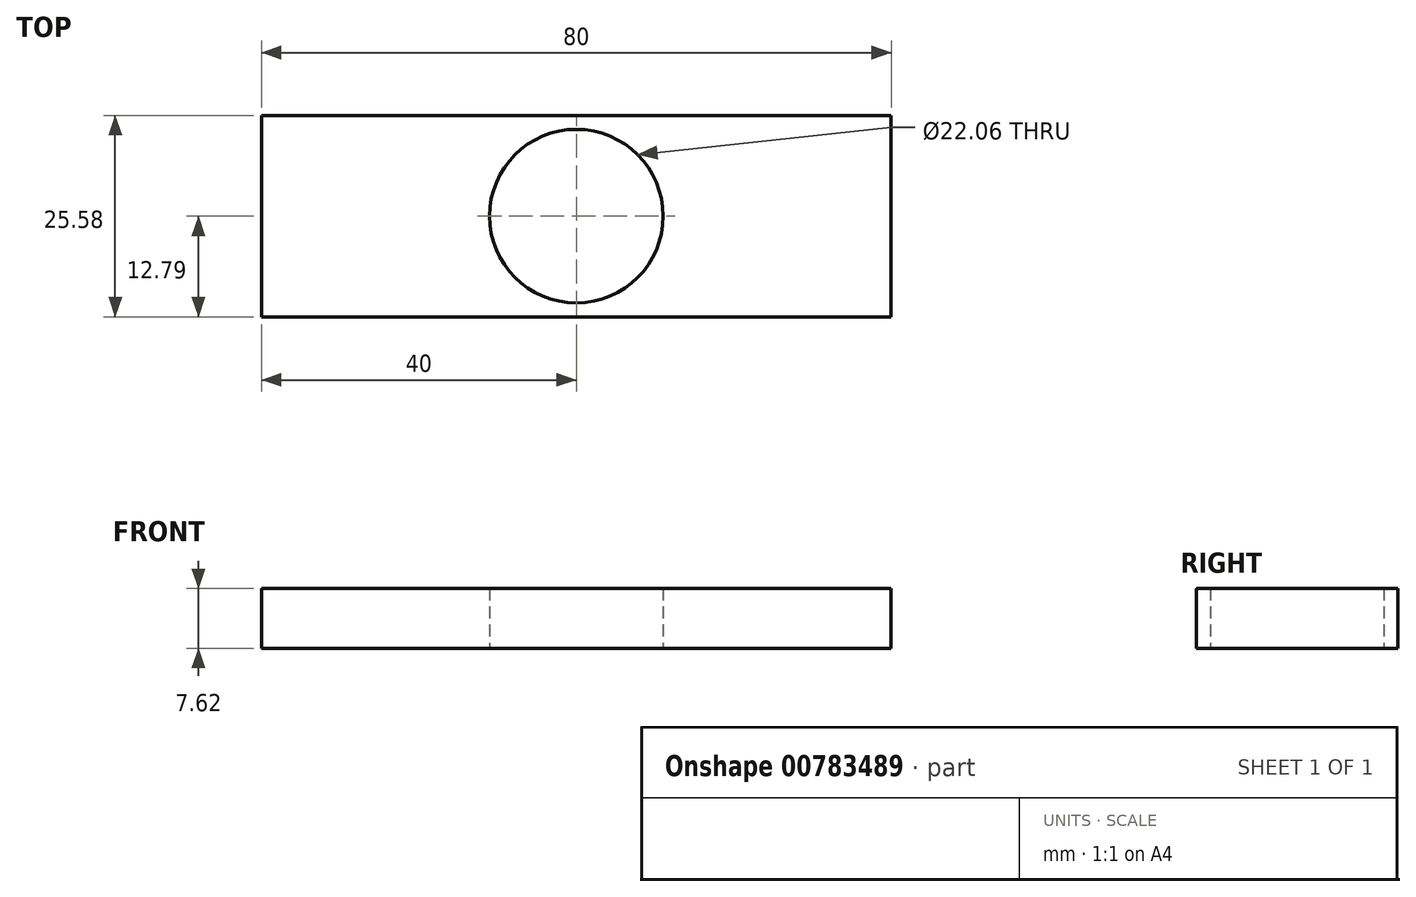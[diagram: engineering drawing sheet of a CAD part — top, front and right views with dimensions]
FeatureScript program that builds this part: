
annotation { "Feature Type Name" : "Feature", "Feature Type Description" : "" }
export const myFeature = defineFeature(function(context is Context, id is Id, definition is map)
    precondition{}
    {
        {
            var Q0;
            Q0=qCreatedBy(makeId("Top.planeOp"),FACE);
            var sketch = newSketch(context, id + "F0", { "sketchPlane" : qUnion([Q0])});
            skLineSegment(sketch, "E0.bottom", {"start": v(40, 12.79) * mm, "end": v(-40, 12.79) * mm});
            skLineSegment(sketch, "E0.top", {"start": v(40, -12.79) * mm, "end": v(-40, -12.79) * mm});
            skLineSegment(sketch, "E0.left", {"start": v(40, 12.79) * mm, "end": v(40, -12.79) * mm});
            skLineSegment(sketch, "E0.right", {"start": v(-40, 12.79) * mm, "end": v(-40, -12.79) * mm});
            skPoint(sketch, "E0.middle", {"position": v(0, 0) * mm});
            skSolve(sketch);
        }
        {
            var Q0;
            Q0 = qSketchRegion(id + "F0", true);
            extrude(context, id + "F1", {"entities" : qUnion([Q0]), "depth" : 7.62 * mm, "offsetDistance" : 25.4 * mm});
        }
        {
            var Q0;
            Q0=sQuery(id+"F0.wireOp",VERTEX,"E0.middle");
            var Q1;
            Q1=makeQuery(id+"F1.opExtrude","SWEPT_BODY",BODY,{"disambiguationData":[OSD([sQuery(id+"F0.wireOp",EDGE,"E0.bottom"),sQuery(id+"F0.wireOp",EDGE,"E0.top"),sQuery(id+"F0.wireOp",EDGE,"E0.left"),sQuery(id+"F0.wireOp",EDGE,"E0.right")])]});
            hole(context, id + "F2", {"style" : HoleStyle.SIMPLE, "endStyle" : HoleEndStyle.THROUGH, "oppositeDirection" : true, "holeDiameter" : 22.06 * mm, "majorDiameter" : 6.35 * mm, "isTappedThrough" : true, "tappedDepth" : 12.7 * mm, "tapClearance" : 3, "locations" : qUnion([Q0]), "scope" : qUnion([Q1])});
        }
    });
